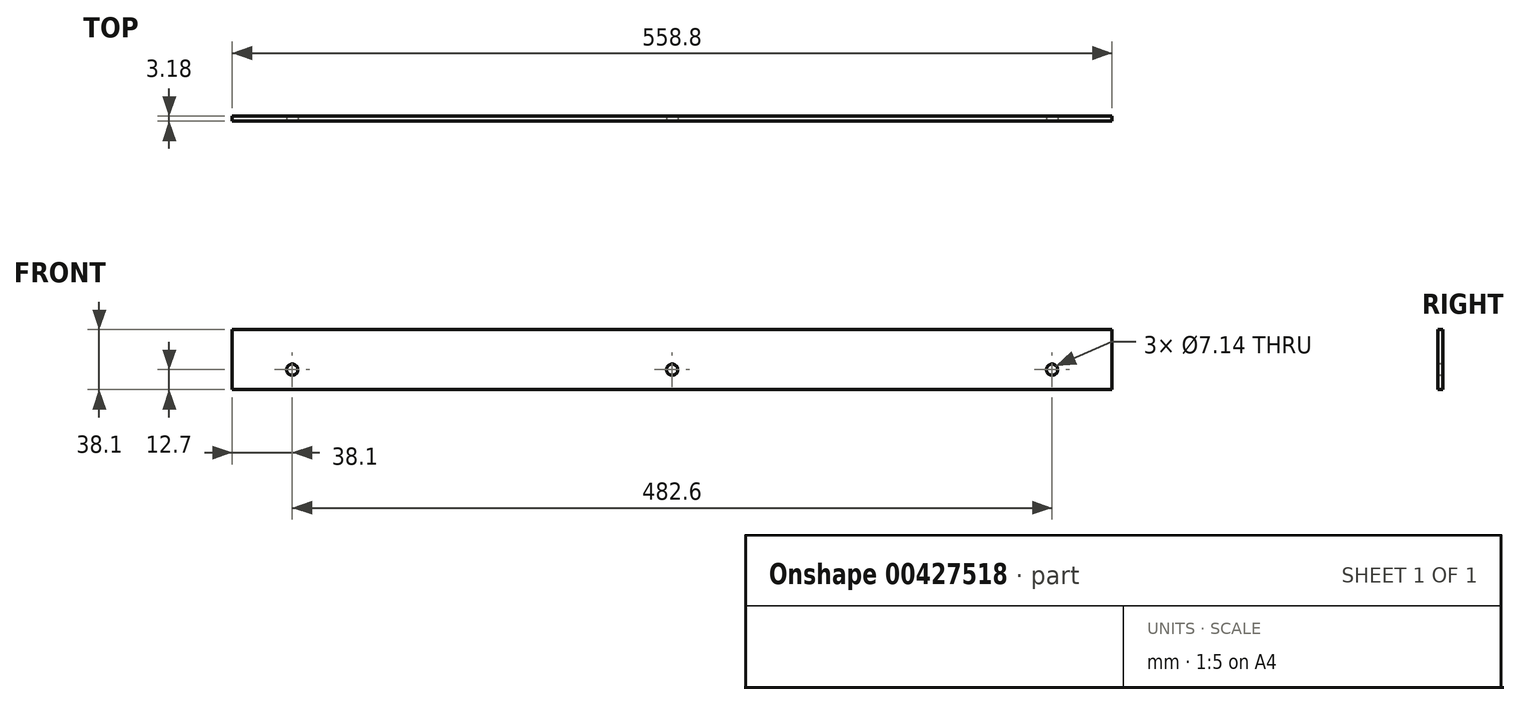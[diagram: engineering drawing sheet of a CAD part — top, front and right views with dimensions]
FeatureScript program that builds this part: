
annotation { "Feature Type Name" : "Feature", "Feature Type Description" : "" }
export const myFeature = defineFeature(function(context is Context, id is Id, definition is map)
    precondition{}
    {
        {
            var Q0;
            Q0=qCreatedBy(makeId("Front.planeOp"),FACE);
            var sketch = newSketch(context, id + "F0", { "sketchPlane" : qUnion([Q0])});
            skLineSegment(sketch, "E0.bottom", {"start": v(0, 0) * mm, "end": v(558.8, 0) * mm});
            skLineSegment(sketch, "E0.top", {"start": v(0, 38.1) * mm, "end": v(558.8, 38.1) * mm});
            skLineSegment(sketch, "E0.left", {"start": v(0, 0) * mm, "end": v(0, 38.1) * mm});
            skLineSegment(sketch, "E0.right", {"start": v(558.8, 0) * mm, "end": v(558.8, 38.1) * mm});
            skSolve(sketch);
        }
        {
            var Q0;
            Q0=makeQuery(id+"F0.imprint","IMPRINT",FACE,{"disambiguationData":[TD([[makeQuery(id+"F0.imprint","IMPRINT",EDGE,{"derivedFrom":sQuery(id+"F0.wireOp",EDGE,"E0.bottom")}),1.0]])]});
            extrude(context, id + "F1", {"entities" : qUnion([Q0]), "oppositeDirection" : true, "depth" : 3.17 * mm});
        }
        {
            var Q0;
            Q0=makeQuery(id+"F1.opExtrude","CAP_FACE",FACE,{"disambiguationData":[OSD([sQuery(id+"F0.wireOp",EDGE,"E0.bottom"),sQuery(id+"F0.wireOp",EDGE,"E0.top"),sQuery(id+"F0.wireOp",EDGE,"E0.left"),sQuery(id+"F0.wireOp",EDGE,"E0.right")])],"isStart":true});
            var sketch = newSketch(context, id + "F2", { "sketchPlane" : qUnion([Q0])});
            skCircle(sketch, "E1", {"center": v(38.1, 12.7) * mm, "radius": 3.57 * mm});
            skCircle(sketch, "E2.1.0.0", {"center": v(279.4, 12.7) * mm, "radius": 3.57 * mm});
            skCircle(sketch, "E2.2.0.0", {"center": v(520.7, 12.7) * mm, "radius": 3.57 * mm});
            skLineSegment(sketch, "E2.direction1", {"start": v(38.1, 12.7) * mm, "end": v(279.4, 12.7) * mm, "construction": true});
            skSolve(sketch);
        }
        {
            var Q0;
            Q0=makeQuery(id+"F2.imprint","IMPRINT",FACE,{"disambiguationData":[TD([[makeQuery(id+"F2.imprint","IMPRINT",EDGE,{"derivedFrom":sQuery(id+"F2.wireOp",EDGE,"E1")}),1.0]])]});
            var Q1;
            Q1=makeQuery(id+"F2.imprint","IMPRINT",FACE,{"disambiguationData":[TD([[makeQuery(id+"F2.imprint","IMPRINT",EDGE,{"derivedFrom":sQuery(id+"F2.wireOp",EDGE,"E2.1.0.0")}),1.0]])]});
            var Q2;
            Q2=makeQuery(id+"F2.imprint","IMPRINT",FACE,{"disambiguationData":[TD([[makeQuery(id+"F2.imprint","IMPRINT",EDGE,{"derivedFrom":sQuery(id+"F2.wireOp",EDGE,"E2.2.0.0")}),1.0]])]});
            extrude(context, id + "F3", {"entities" : qUnion([Q0, Q1, Q2]), "operationType" : NewBodyOperationType.REMOVE, "endBound" : BoundingType.THROUGH_ALL, "oppositeDirection" : true, "depth" : 25.4 * mm});
        }
    });
